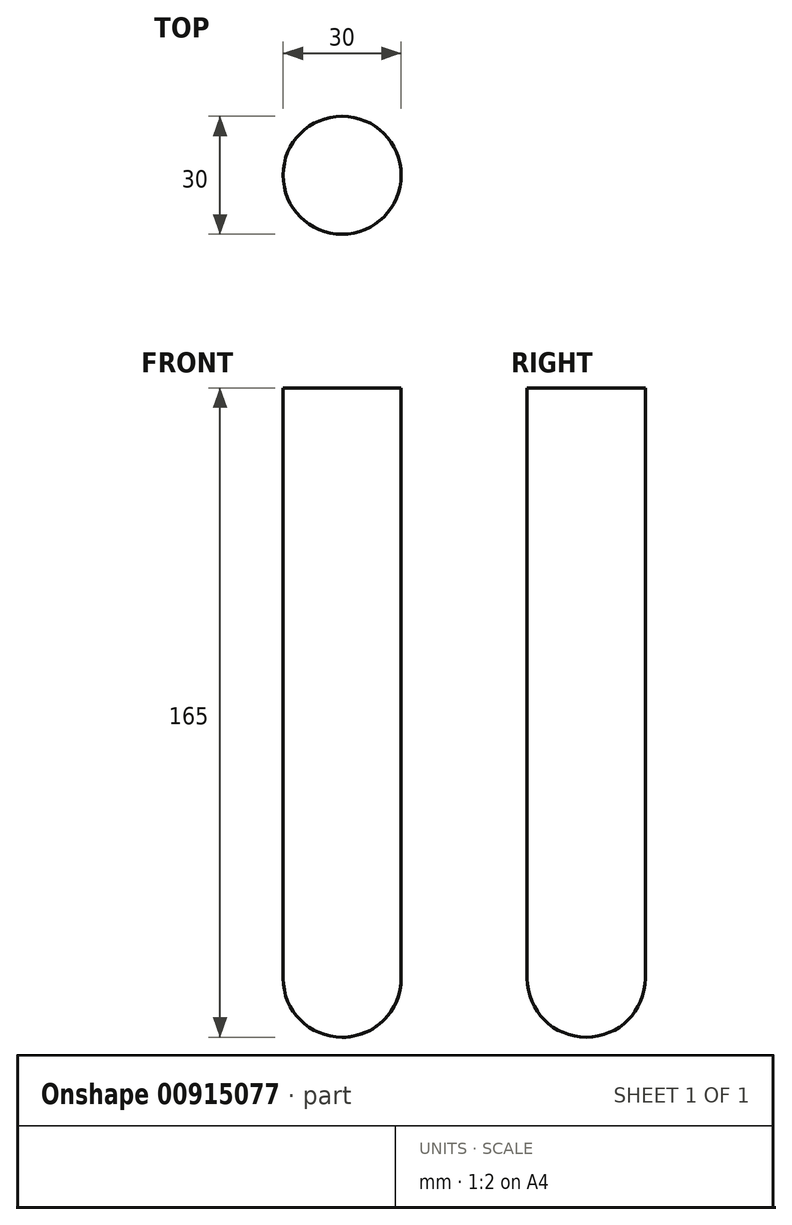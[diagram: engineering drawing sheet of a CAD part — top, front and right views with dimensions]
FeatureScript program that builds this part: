
annotation { "Feature Type Name" : "Feature", "Feature Type Description" : "" }
export const myFeature = defineFeature(function(context is Context, id is Id, definition is map)
    precondition{}
    {
        {
            var Q0;
            Q0=qCreatedBy(makeId("Front.planeOp"),FACE);
            var sketch = newSketch(context, id + "F0", { "sketchPlane" : qUnion([Q0])});
            skLineSegment(sketch, "E0", {"start": v(0, 165) * mm, "end": v(0, 0) * mm});
            skLineSegment(sketch, "E1", {"start": v(0, 165) * mm, "end": v(15, 165) * mm});
            skLineSegment(sketch, "E2", {"start": v(15, 165) * mm, "end": v(15, 15) * mm});
            skArc(sketch, "E3", {"start": v(15, 15) * mm, "mid": v(10.6, 4.4) * mm, "end": v(0, 0) * mm});
            skSolve(sketch);
        }
        {
            var Q0;
            Q0 = qSketchRegion(id + "F0", true);
            var Q1;
            Q1=sQuery(id+"F0.wireOp",EDGE,"E0");
            revolve(context, id + "F1", {"surfaceOperationType" : NewSurfaceOperationType.NEW, "entities" : qUnion([Q0]), "axis" : qUnion([Q1]), "revolveType" : RevolveType.FULL});
        }
    });
